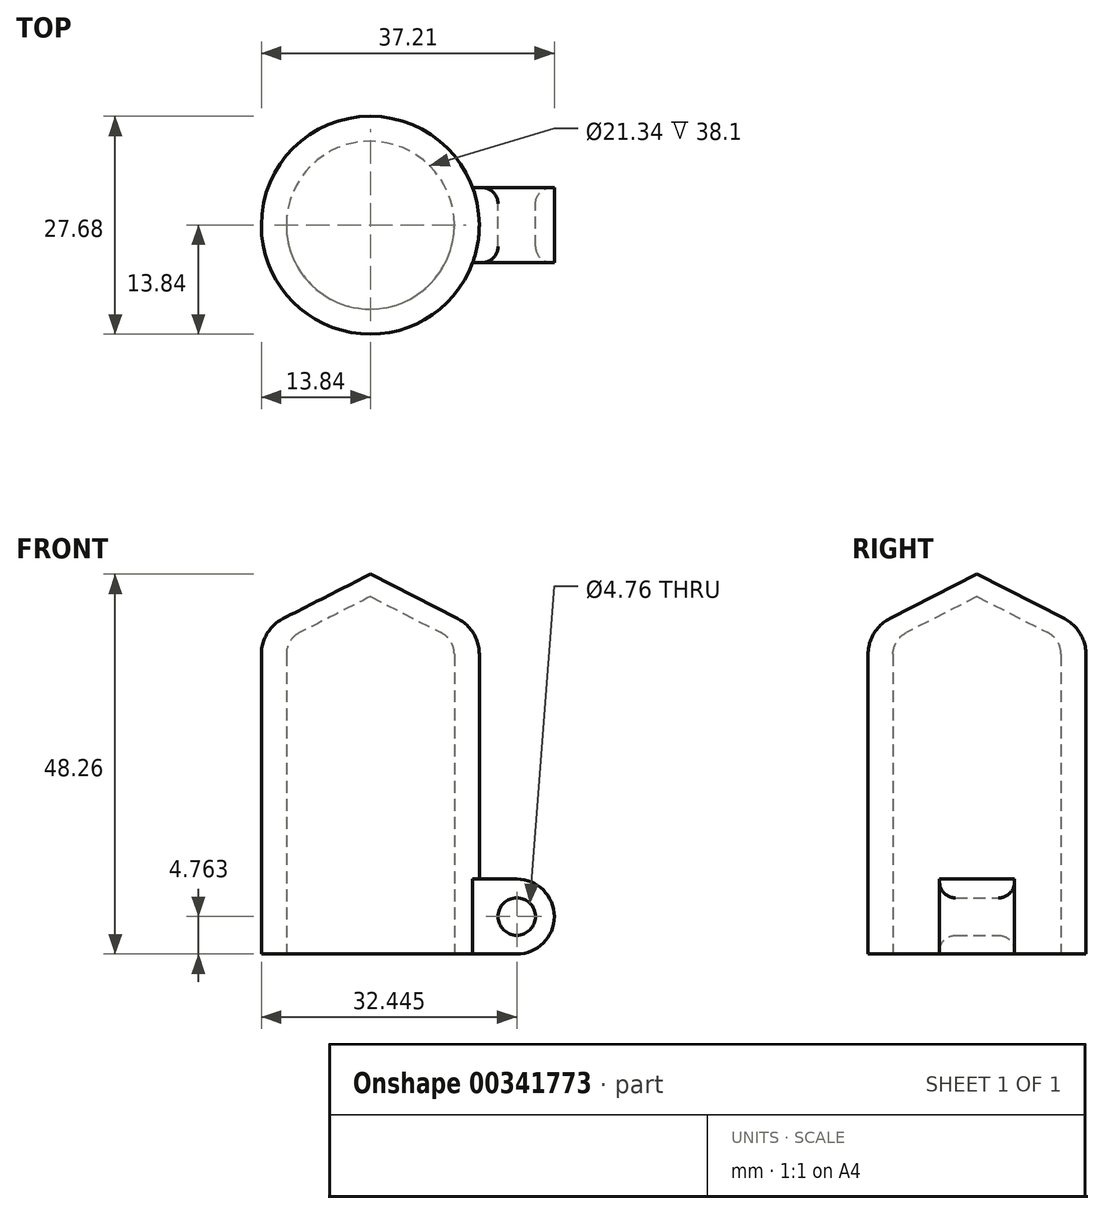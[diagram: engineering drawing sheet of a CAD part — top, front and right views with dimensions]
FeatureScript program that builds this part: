
annotation { "Feature Type Name" : "Feature", "Feature Type Description" : "" }
export const myFeature = defineFeature(function(context is Context, id is Id, definition is map)
    precondition{}
    {
        {
            var Q0;
            Q0=qCreatedBy(makeId("Top.planeOp"),FACE);
            var sketch = newSketch(context, id + "F0", { "sketchPlane" : qUnion([Q0])});
            skCircle(sketch, "E0", {"center": v(0, 0) * mm, "radius": 10.67 * mm});
            skCircle(sketch, "E1.0", {"center": v(0, 0) * mm, "radius": 13.84 * mm});
            skSolve(sketch);
        }
        {
            var Q0;
            Q0 = qSketchRegion(id + "F0", true);
            extrude(context, id + "F1", {"entities" : qUnion([Q0]), "depth" : 38.1 * mm});
        }
        {
            var Q0;
            Q0=qCreatedBy(makeId("Front.planeOp"),FACE);
            var sketch = newSketch(context, id + "F2", { "sketchPlane" : qUnion([Q0])});
            skLineSegment(sketch, "E2", {"start": v(13.84, 0) * mm, "end": v(13.84, 9.53) * mm, "construction": true});
            skCircle(sketch, "E3", {"center": v(18.6, 4.76) * mm, "radius": 4.76 * mm});
            skLineSegment(sketch, "E4", {"start": v(18.6, 9.53) * mm, "end": v(13.84, 9.53) * mm});
            skLineSegment(sketch, "E5", {"start": v(18.6, 0) * mm, "end": v(13.84, 0) * mm});
            skLineSegment(sketch, "E6", {"start": v(13.84, 9.53) * mm, "end": v(11.3, 9.53) * mm});
            skLineSegment(sketch, "E7", {"start": v(11.3, 9.53) * mm, "end": v(11.3, 0) * mm});
            skLineSegment(sketch, "E8", {"start": v(11.3, 0) * mm, "end": v(13.84, 0) * mm});
            skLineSegment(sketch, "E9.0", {"start": v(-13.84, 0) * mm, "end": v(13.84, 0) * mm});
            skCircle(sketch, "E10", {"center": v(18.6, 4.76) * mm, "radius": 2.38 * mm});
            skSolve(sketch);
        }
        {
            var Q0;
            {var subQ1=sQuery(id+"F2.wireOp",EDGE,"E4");Q0=makeQuery(id+"F2.imprint","IMPRINT",FACE,{"disambiguationData":[TD([[makeQuery(id+"F2.imprint","IMPRINT",EDGE,{"derivedFrom":subQ1}),1.0]])]});}
            var Q1;
            {var subQ0=sQuery(id+"F2.wireOp",EDGE,"E3");var subQ1=makeQuery(id+"F2.imprint","INTERSECT",VERTEX,{"derivedFrom":[subQ0,sQuery(id+"F2.wireOp",EDGE,"E4")]});Q1=makeQuery(id+"F2.imprint","IMPRINT",FACE,{"disambiguationData":[TD([[makeQuery(id+"F2.imprint","IMPRINT",EDGE,{"disambiguationData":[TD([[subQ1,-1.0]])],"derivedFrom":subQ0}),1.0]])]});}
            extrude(context, id + "F3", {"entities" : qUnion([Q0, Q1]), "operationType" : NewBodyOperationType.ADD, "endBound" : BoundingType.SYMMETRIC, "depth" : 9.52 * mm});
        }
        {
            var Q0;
            Q0=makeQuery(id+"F3.opExtrude","CAP_EDGE",EDGE,{"disambiguationData":[OSD([sQuery(id+"F2.wireOp",EDGE,"E10")])],"isStart":false});
            var Q1;
            Q1=makeQuery(id+"F3.opExtrude","CAP_EDGE",EDGE,{"disambiguationData":[OSD([sQuery(id+"F2.wireOp",EDGE,"E10")])],"isStart":true});
            fillet(context, id + "F4", {"entities" : qUnion([Q0, Q1]), "radius" : 2.03 * mm, "tangentPropagation" : true, "allowEdgeOverflow" : false});
        }
        {
            var Q0;
            Q0=qCreatedBy(makeId("Front.planeOp"),FACE);
            var sketch = newSketch(context, id + "F5", { "sketchPlane" : qUnion([Q0])});
            skLineSegment(sketch, "E11.0", {"start": v(-13.84, 38.1) * mm, "end": v(13.84, 38.1) * mm, "construction": true});
            skArc(sketch, "E12", {"start": v(-11.07, 42.63) * mm, "mid": v(-13.1, 40.76) * mm, "end": v(-13.84, 38.1) * mm});
            skLineSegment(sketch, "E13", {"start": v(-11.07, 42.63) * mm, "end": v(0, 48.26) * mm});
            skLineSegment(sketch, "E14.0", {"start": v(-9, 40.83) * mm, "end": v(0, 45.4) * mm});
            skArc(sketch, "E15", {"start": v(-9, 40.83) * mm, "mid": v(-10.22, 39.7) * mm, "end": v(-10.67, 38.1) * mm});
            skLineSegment(sketch, "E16", {"start": v(0, 48.26) * mm, "end": v(0, 45.4) * mm});
            skLineSegment(sketch, "E17", {"start": v(-13.84, 38.1) * mm, "end": v(-10.67, 38.1) * mm});
            skSolve(sketch);
        }
        {
            var Q0;
            Q0=makeQuery(id+"F5.imprint","IMPRINT",FACE,{"disambiguationData":[TD([[makeQuery(id+"F5.imprint","IMPRINT",EDGE,{"derivedFrom":sQuery(id+"F5.wireOp",EDGE,"E12")}),1.0]])]});
            var Q1;
            Q1=makeQuery(id+"F1.opExtrude","SWEPT_FACE",FACE,{"disambiguationData":[OSD([sQuery(id+"F0.wireOp",EDGE,"E0")])]});
            revolve(context, id + "F6", {"operationType" : NewBodyOperationType.ADD, "entities" : qUnion([Q0]), "axis" : qUnion([Q1]), "revolveType" : RevolveType.FULL});
        }
    });
